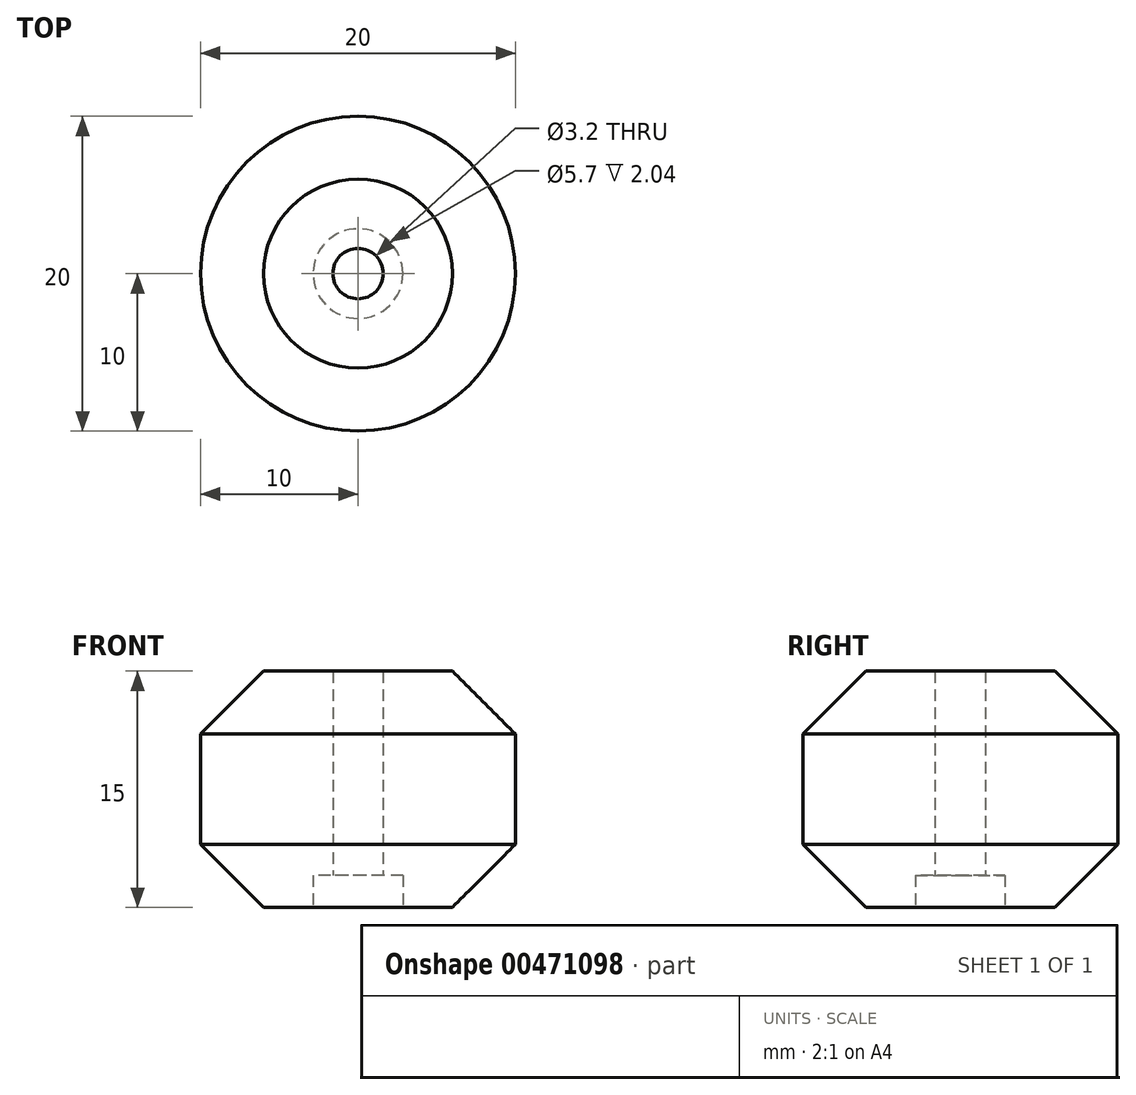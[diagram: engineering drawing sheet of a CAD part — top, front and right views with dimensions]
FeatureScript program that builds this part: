
annotation { "Feature Type Name" : "Feature", "Feature Type Description" : "" }
export const myFeature = defineFeature(function(context is Context, id is Id, definition is map)
    precondition{}
    {
        {
            var Q0;
            Q0=qCreatedBy(makeId("Top.planeOp"),FACE);
            var sketch = newSketch(context, id + "F0", { "sketchPlane" : qUnion([Q0])});
            skCircle(sketch, "E0", {"center": v(0, 0) * mm, "radius": 1.6 * mm});
            skCircle(sketch, "E1", {"center": v(0, 0) * mm, "radius": 10 * mm});
            skCircle(sketch, "E2", {"center": v(0, 0) * mm, "radius": 2.85 * mm});
            skSolve(sketch);
        }
        {
            var Q0;
            Q0 = qSketchRegion(id + "F0", true);
            var Q1;
            Q1=makeQuery(id+"F0.imprint","IMPRINT",FACE,{"disambiguationData":[TD([[makeQuery(id+"F0.imprint","IMPRINT",EDGE,{"derivedFrom":sQuery(id+"F0.wireOp",EDGE,"E0")}),-1.0]])]});
            extrude(context, id + "F1", {"entities" : qUnion([Q0, Q1]), "depth" : 15 * mm, "offsetDistance" : 25 * mm});
        }
        {
            var Q0;
            Q0=makeQuery(id+"F1.opExtrude","SWEPT_FACE",FACE,{"disambiguationData":[OSD([sQuery(id+"F0.wireOp",EDGE,"E1")])]});
            chamfer(context, id + "F2", {"entities" : qUnion([Q0]), "width" : 4 * mm, "tangentPropagation" : true});
        }
        {
            var Q0;
            Q0=makeQuery(id+"F0.imprint","IMPRINT",FACE,{"disambiguationData":[TD([[makeQuery(id+"F0.imprint","IMPRINT",EDGE,{"derivedFrom":sQuery(id+"F0.wireOp",EDGE,"E0")}),-1.0]])]});
            extrude(context, id + "F3", {"entities" : qUnion([Q0]), "operationType" : NewBodyOperationType.REMOVE, "depth" : 2.04 * mm, "offsetDistance" : 25 * mm});
        }
    });
